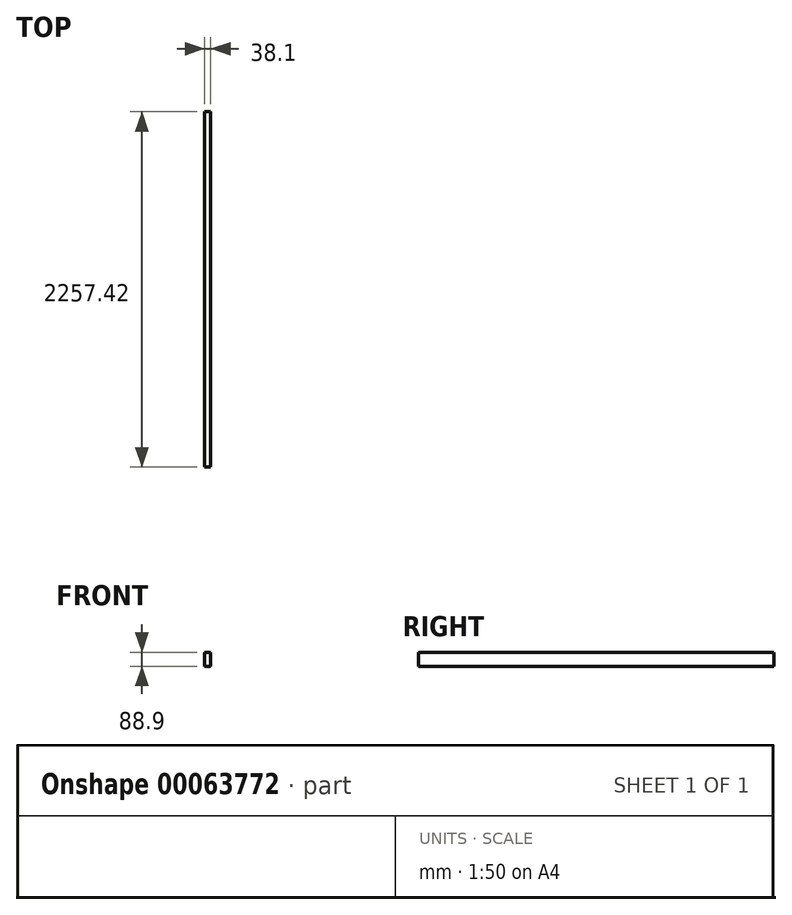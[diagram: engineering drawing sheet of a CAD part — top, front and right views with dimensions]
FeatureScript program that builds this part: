
annotation { "Feature Type Name" : "Feature", "Feature Type Description" : "" }
export const myFeature = defineFeature(function(context is Context, id is Id, definition is map)
    precondition{}
    {
        {
            var Q0;
            Q0=qCreatedBy(makeId("Front.planeOp"),FACE);
            var sketch = newSketch(context, id + "F0", { "sketchPlane" : qUnion([Q0])});
            skLineSegment(sketch, "E0.bottom", {"start": v(-18, 55.77) * mm, "end": v(20.1, 55.77) * mm});
            skLineSegment(sketch, "E0.top", {"start": v(-18, -33.13) * mm, "end": v(20.1, -33.13) * mm});
            skLineSegment(sketch, "E0.left", {"start": v(-18, 55.77) * mm, "end": v(-18, -33.13) * mm});
            skLineSegment(sketch, "E0.right", {"start": v(20.1, 55.77) * mm, "end": v(20.1, -33.13) * mm});
            skSolve(sketch);
        }
        {
            var Q0;
            Q0=qSketchRegion(id+"F0",true);
            extrude(context, id + "F1", {"entities" : qUnion([Q0]), "endBound" : BoundingType.SYMMETRIC, "depth" : 2257.42 * mm});
        }
    });
